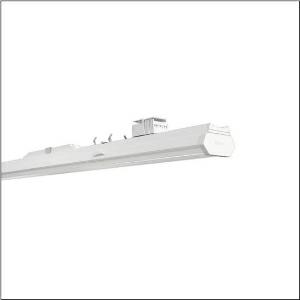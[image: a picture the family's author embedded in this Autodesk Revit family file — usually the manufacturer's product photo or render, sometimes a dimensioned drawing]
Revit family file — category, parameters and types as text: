
# Revit family: licross_r__11_protected_ho_51tp12dn4fxmd_e40f
name_source: partatom
category: Lighting Fixtures
units: mm (PartAtom-declared; Revit-internal decimal feet)

## family parameters
Cut with Voids When Loaded = No
Host = Face
Light Source = No
Part Type = Normal
Room Calculation Point = No
Round Connector Dimension = Use Diameter
Shared = No

## types (1)
- --- (1 x LED, 2290 lm, 13.9 W, 4000K)
    Apparent Load = 14 VA
    CIE Flux Codes = 70 91 97 98 100
    Color Rendering = 80
    Color Temperature = 4000K
    Default Elevation = 1800 mm
    Description = Licross® 11 Protected HO, luminaire insert, of sheet steel, galvanised, coil coated, white, length: 1.500mm, width: 90mm, height: 101mm, LED rated luminous flux: 15.270lm, light colour: 840, control gear: DALI 2 (for two DALI lines), with plug, 6-pole, with phase selection, mains connection: 220..240V, AC/DC, 0/50..60Hz, rated input power: 87W, halogen-free wiring, for central battery installations according to DIN EN 60598-2-22, for emergency light function, without changeover relay, primary optical cover: cover, of PMMA, light emission: direct distribution, primary light characteristic: symmetric, protection rating (complete): IP64, insulation class (complete): insulation class I (protective earthing), certification: CE, ENEC, VDE, UKCA, protection symbol: D if used in an environment with conductive dust loads with corresponding accessories, impact resistance: IK06, permissible ambient temperature for indoor applications: -25..+30°C, standard: EN 60598-2-22, corresponds to IFS (International Featured Standards) requirements for safety and quality in the food industry, reducing of maximum allowable ambient temperature of 5°C with ceiling mounting, LABS conformity tested according to VDMA 24364:2018-05, packaging unit: 1 piece
    Height = 92 mm
    Lamp = 1 x LED
    Lamp Light Flux = 2290 lm
    Lamp Power = 13.9 W
    Lamp count = 1
    Length = 1500 mm
    Luminous efficacy = 165 lm/W
    Manufacturer = Siteco
    ModVariant = No
    Model = 51TP12DN4FXMD
    Mounting Place = Ceiling
    Mounting Type = Pendant
    Number of Poles = 1
    OnlyDefault = Yes
    Power Factor = 1
    Product Name = Licross® 11 Protected HO
    Product group = luminaire insert
    ProductGroupID = 902
    Protection Class = Protection class I
    Protection Degree = IP 64
    RLX_Detail_Level = 1
    RLX_Emergency_Light_Flux = 0 lm
    RLX_Emergency_Type = 0
    RLX_Emergency_Type_DB = No
    RlxData = <blob elided: 24781 chars, md5=e9f52a1b>
    Socket = socket
    Standby Power = 0 W
    System Light Flux = 2290 lm
    System Power = 14 W
    Type Comments = : DC mode (central or group accumulator) initial emergency light level
    Type Image = l_1256148.jpg
    URL = http://relux.com
    VarID = @adj_087642
    Voltage = 0 V
    Weight = 0.00 kg
    Width = 88 mm

## geometry (parser evidence)
native form markers: Blend x4, Sweep x9
no freeform markers — native parametric forms only
